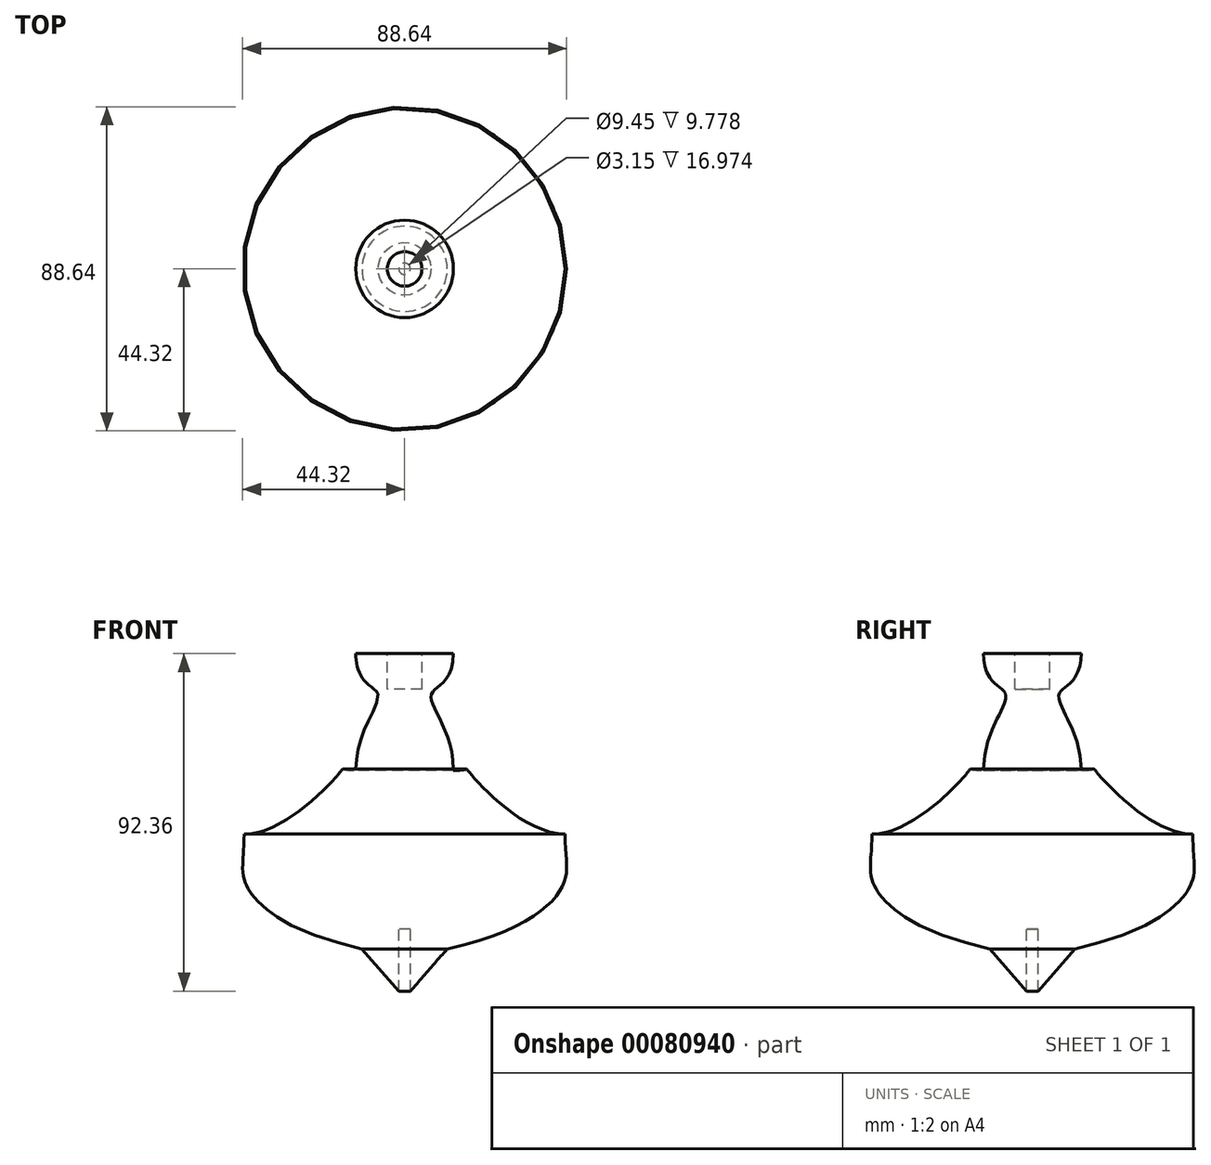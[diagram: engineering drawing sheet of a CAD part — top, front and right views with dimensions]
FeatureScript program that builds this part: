
annotation { "Feature Type Name" : "Feature", "Feature Type Description" : "" }
export const myFeature = defineFeature(function(context is Context, id is Id, definition is map)
    precondition{}
    {
        {
            var Q0;
            Q0=qCreatedBy(makeId("Front.planeOp"),FACE);
            var sketch = newSketch(context, id + "F0", { "sketchPlane" : qUnion([Q0])});
            skLineSegment(sketch, "E0", {"start": v(0, 32) * mm, "end": v(-13.34, 32) * mm});
            skFitSpline(sketch, "E1", {"points": [v(-43.9, -17.42) * mm, v(-43.9, -29.66) * mm, v(-11.67, -48.82) * mm], "startDerivative": vector(0, -51.6) * mm, "endDerivative": vector(109.42, -24.84) * mm});
            skLineSegment(sketch, "E2", {"start": v(-11.67, -48.82) * mm, "end": v(-1.57, -60.37) * mm});
            skLineSegment(sketch, "E3", {"start": v(0, 22.21) * mm, "end": v(0, -43.4) * mm});
            skFitSpline(sketch, "E4", {"points": [v(-13.34, 32) * mm, v(-7.32, 20.87) * mm, v(-13.34, 0) * mm], "startDerivative": vector(0, -58.32) * mm, "endDerivative": vector(0, -58.32) * mm});
            skFitSpline(sketch, "E5", {"points": [v(-13.34, 0) * mm, v(-17.28, 0) * mm, v(-43.9, -17.42) * mm], "startDerivative": vector(-47.78, 0) * mm, "endDerivative": vector(-47.78, 0) * mm});
            skLineSegment(sketch, "E6", {"start": v(0, 22.21) * mm, "end": v(-4.72, 22.21) * mm});
            skLineSegment(sketch, "E7", {"start": v(-4.72, 22.21) * mm, "end": v(-4.72, 32) * mm});
            skLineSegment(sketch, "E8", {"start": v(-1.57, -60.37) * mm, "end": v(-1.57, -43.4) * mm});
            skLineSegment(sketch, "E9", {"start": v(-1.57, -43.4) * mm, "end": v(0, -43.4) * mm});
            skPoint(sketch, "E10.orphan", {"position": v(0, -62.18) * mm});
            skSolve(sketch);
        }
        {
            var Q0;
            Q0=makeQuery(id+"F0.imprint","IMPRINT",FACE,{"disambiguationData":[TD([[makeQuery(id+"F0.imprint","IMPRINT",EDGE,{"derivedFrom":sQuery(id+"F0.wireOp",EDGE,"E0")}),1.0]])]});
            var Q1;
            Q1=sQuery(id+"F0.wireOp",EDGE,"E0");
            var Q2;
            Q2=sQuery(id+"F0.wireOp",EDGE,"E4");
            var Q3;
            Q3=sQuery(id+"F0.wireOp",EDGE,"E5");
            var Q4;
            Q4=sQuery(id+"F0.wireOp",EDGE,"E1");
            var Q5;
            Q5=sQuery(id+"F0.wireOp",EDGE,"E2");
            var Q6;
            Q6=sQuery(id+"F0.wireOp",EDGE,"E2");
            var Q7;
            Q7=sQuery(id+"F0.wireOp",EDGE,"E3");
            revolve(context, id + "F1", {"entities" : qUnion([Q0]), "surfaceEntities" : qUnion([Q1, Q2, Q3, Q4, Q5, Q6]), "axis" : qUnion([Q7]), "revolveType" : RevolveType.FULL});
        }
    });
